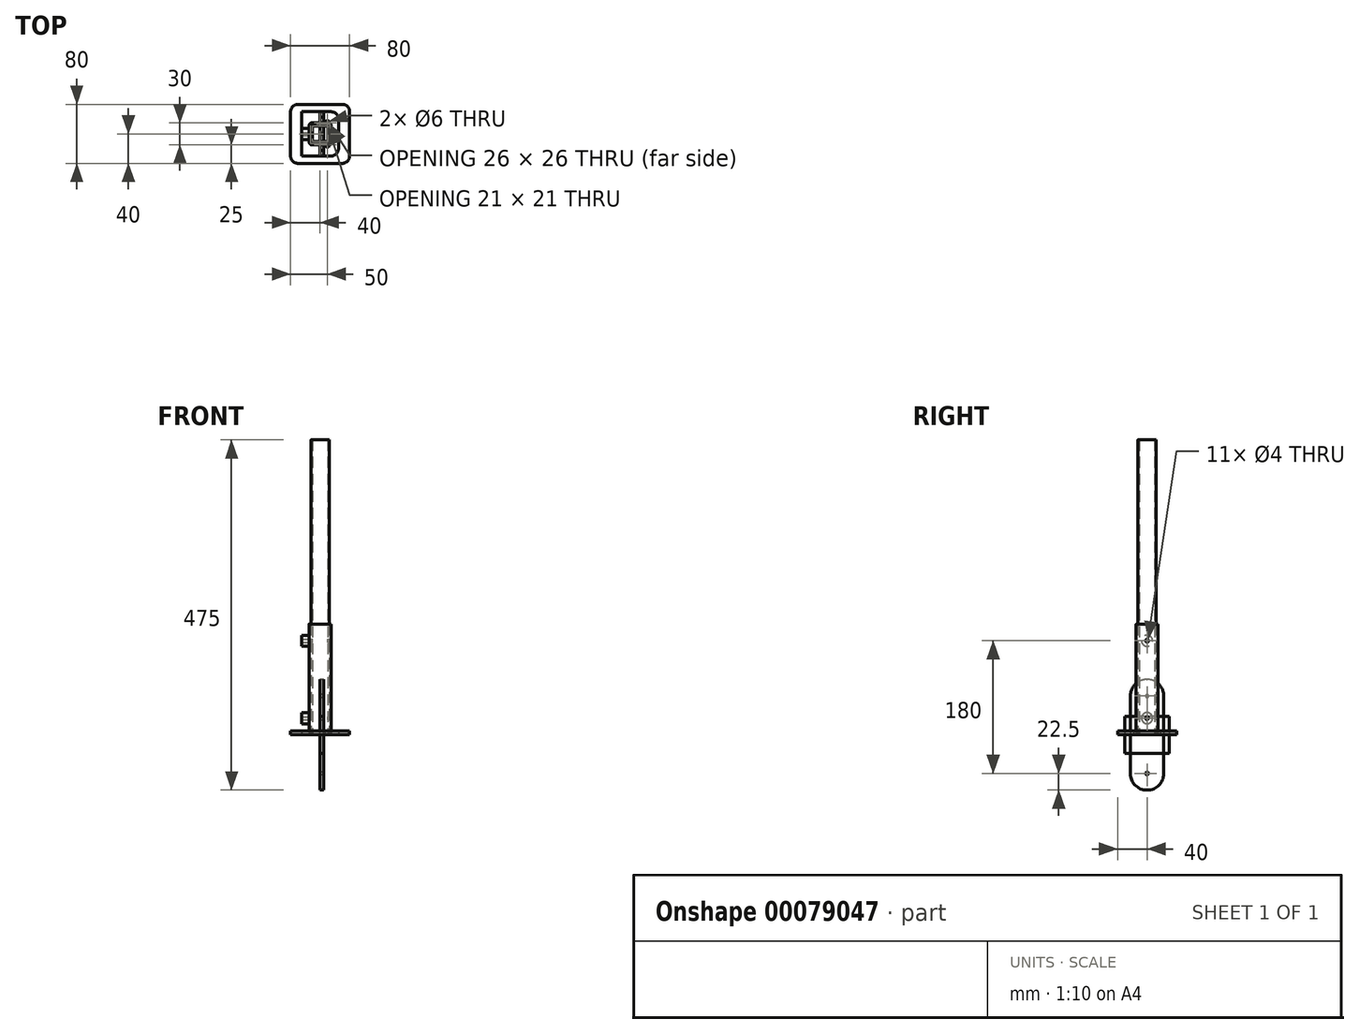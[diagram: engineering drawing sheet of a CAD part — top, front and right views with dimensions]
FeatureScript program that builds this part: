
annotation { "Feature Type Name" : "Feature", "Feature Type Description" : "" }
export const myFeature = defineFeature(function(context is Context, id is Id, definition is map)
    precondition{}
    {
        {
            var Q0;
            Q0=qCreatedBy(makeId("Top.planeOp"),FACE);
            var sketch = newSketch(context, id + "F0", { "sketchPlane" : qUnion([Q0])});
            skLineSegment(sketch, "E0.bottom", {"start": v(-30, -40) * mm, "end": v(30, -40) * mm});
            skLineSegment(sketch, "E0.top", {"start": v(-30, 40) * mm, "end": v(30, 40) * mm});
            skLineSegment(sketch, "E0.left", {"start": v(-40, -30) * mm, "end": v(-40, 30) * mm});
            skLineSegment(sketch, "E0.right", {"start": v(40, -30) * mm, "end": v(40, 30) * mm});
            skLineSegment(sketch, "E1", {"start": v(-40, 40) * mm, "end": v(40, -40) * mm, "construction": true});
            skPoint(sketch, "E2.visualSharp", {"position": v(40, 40) * mm});
            skArc(sketch, "E2.filletArc", {"start": v(40, 30) * mm, "mid": v(37.07, 37.07) * mm, "end": v(30, 40) * mm});
            skPoint(sketch, "E3.visualSharp", {"position": v(40, -40) * mm});
            skArc(sketch, "E3.filletArc", {"start": v(30, -40) * mm, "mid": v(37.07, -37.07) * mm, "end": v(40, -30) * mm});
            skPoint(sketch, "E4.visualSharp", {"position": v(-40, -40) * mm});
            skArc(sketch, "E4.filletArc", {"start": v(-40, -30) * mm, "mid": v(-37.07, -37.07) * mm, "end": v(-30, -40) * mm});
            skPoint(sketch, "E5.visualSharp", {"position": v(-40, 40) * mm});
            skArc(sketch, "E5.filletArc", {"start": v(-30, 40) * mm, "mid": v(-37.07, 37.07) * mm, "end": v(-40, 30) * mm});
            skSolve(sketch);
        }
        {
            var Q0;
            Q0=makeQuery(id+"F0.imprint","IMPRINT",FACE,{"disambiguationData":[TD([[makeQuery(id+"F0.imprint","IMPRINT",EDGE,{"derivedFrom":sQuery(id+"F0.wireOp",EDGE,"E0.bottom")}),1.0]])]});
            extrude(context, id + "F1", {"entities" : qUnion([Q0]), "depth" : 5 * mm});
        }
        {
            var Q0;
            Q0=qCreatedBy(makeId("Right.planeOp"),FACE);
            var sketch = newSketch(context, id + "F2", { "sketchPlane" : qUnion([Q0])});
            skLineSegment(sketch, "E6.bottom", {"start": v(30, -25) * mm, "end": v(-30, -25) * mm});
            skLineSegment(sketch, "E6.top", {"start": v(30, 25) * mm, "end": v(-30, 25) * mm});
            skLineSegment(sketch, "E6.left", {"start": v(30, -25) * mm, "end": v(30, 25) * mm});
            skLineSegment(sketch, "E6.right", {"start": v(-30, -25) * mm, "end": v(-30, 25) * mm});
            skLineSegment(sketch, "E7", {"start": v(30, 25) * mm, "end": v(-30, -25) * mm, "construction": true});
            skSolve(sketch);
        }
        {
            var Q0;
            Q0 = qSketchRegion(id + "F2", true);
            extrude(context, id + "F3", {"entities" : qUnion([Q0]), "depth" : 5 * mm});
        }
        {
            var Q0;
            Q0=qCreatedBy(makeId("Top.planeOp"),FACE);
            var sketch = newSketch(context, id + "F4", { "sketchPlane" : qUnion([Q0])});
            skLineSegment(sketch, "E8.bottom", {"start": v(15, 30) * mm, "end": v(-25, 30) * mm});
            skLineSegment(sketch, "E8.top", {"start": v(15, -30) * mm, "end": v(-25, -30) * mm});
            skLineSegment(sketch, "E8.left", {"start": v(25, 20) * mm, "end": v(25, -20) * mm});
            skLineSegment(sketch, "E8.right", {"start": v(-25, 30) * mm, "end": v(-25, -30) * mm});
            skLineSegment(sketch, "E9", {"start": v(25, 30) * mm, "end": v(-25, -30) * mm, "construction": true});
            skPoint(sketch, "E10.visualSharp", {"position": v(25, 30) * mm});
            skArc(sketch, "E10.filletArc", {"start": v(25, 20) * mm, "mid": v(22.07, 27.07) * mm, "end": v(15, 30) * mm});
            skPoint(sketch, "E11.visualSharp", {"position": v(25, -30) * mm});
            skArc(sketch, "E11.filletArc", {"start": v(15, -30) * mm, "mid": v(22.07, -27.07) * mm, "end": v(25, -20) * mm});
            skLineSegment(sketch, "E12", {"start": v(10, 30) * mm, "end": v(10, 15) * mm, "construction": true});
            skLineSegment(sketch, "E13", {"start": v(25, 15) * mm, "end": v(10, 15) * mm, "construction": true});
            skLineSegment(sketch, "E14", {"start": v(25, -15) * mm, "end": v(10, -15) * mm, "construction": true});
            skLineSegment(sketch, "E15", {"start": v(10, -30) * mm, "end": v(10, -15) * mm, "construction": true});
            skCircle(sketch, "E16", {"center": v(10, 15) * mm, "radius": 3 * mm});
            skCircle(sketch, "E17", {"center": v(10, -15) * mm, "radius": 3 * mm});
            skSolve(sketch);
        }
        {
            var Q0;
            Q0=makeQuery(id+"F4.imprint","IMPRINT",FACE,{"disambiguationData":[TD([[makeQuery(id+"F4.imprint","IMPRINT",EDGE,{"derivedFrom":sQuery(id+"F4.wireOp",EDGE,"E8.bottom")}),1.0]])]});
            extrude(context, id + "F5", {"entities" : qUnion([Q0]), "depth" : 5 * mm});
        }
        {
            var Q0;
            Q0=qCreatedBy(makeId("Top.planeOp"),FACE);
            var sketch = newSketch(context, id + "F6", { "sketchPlane" : qUnion([Q0])});
            skLineSegment(sketch, "E18.bottom", {"start": v(9.5, 12.5) * mm, "end": v(-9.5, 12.5) * mm});
            skLineSegment(sketch, "E18.top", {"start": v(9.5, -12.5) * mm, "end": v(-9.5, -12.5) * mm});
            skLineSegment(sketch, "E18.left", {"start": v(12.5, 9.5) * mm, "end": v(12.5, -9.5) * mm});
            skLineSegment(sketch, "E18.right", {"start": v(-12.5, 9.5) * mm, "end": v(-12.5, -9.5) * mm});
            skLineSegment(sketch, "E19", {"start": v(12.5, 12.5) * mm, "end": v(-12.5, -12.5) * mm, "construction": true});
            skPoint(sketch, "E20.visualSharp", {"position": v(12.5, 12.5) * mm});
            skArc(sketch, "E20.filletArc", {"start": v(12.5, 9.5) * mm, "mid": v(11.62, 11.62) * mm, "end": v(9.5, 12.5) * mm});
            skPoint(sketch, "E21.visualSharp", {"position": v(-12.5, 12.5) * mm});
            skArc(sketch, "E21.filletArc", {"start": v(-9.5, 12.5) * mm, "mid": v(-11.62, 11.62) * mm, "end": v(-12.5, 9.5) * mm});
            skPoint(sketch, "E22.visualSharp", {"position": v(-12.5, -12.5) * mm});
            skArc(sketch, "E22.filletArc", {"start": v(-12.5, -9.5) * mm, "mid": v(-11.62, -11.62) * mm, "end": v(-9.5, -12.5) * mm});
            skPoint(sketch, "E23.visualSharp", {"position": v(12.5, -12.5) * mm});
            skArc(sketch, "E23.filletArc", {"start": v(9.5, -12.5) * mm, "mid": v(11.62, -11.62) * mm, "end": v(12.5, -9.5) * mm});
            skArc(sketch, "E24.0", {"start": v(10.5, 9.5) * mm, "mid": v(10.2, 10.2) * mm, "end": v(9.5, 10.5) * mm});
            skLineSegment(sketch, "E24.1", {"start": v(9.5, 10.5) * mm, "end": v(-9.5, 10.5) * mm});
            skLineSegment(sketch, "E24.2", {"start": v(10.5, 9.5) * mm, "end": v(10.5, -9.5) * mm});
            skArc(sketch, "E24.3", {"start": v(-9.5, 10.5) * mm, "mid": v(-10.2, 10.2) * mm, "end": v(-10.5, 9.5) * mm});
            skArc(sketch, "E24.4", {"start": v(9.5, -10.5) * mm, "mid": v(10.2, -10.2) * mm, "end": v(10.5, -9.5) * mm});
            skLineSegment(sketch, "E24.5", {"start": v(9.5, -10.5) * mm, "end": v(-9.5, -10.5) * mm});
            skArc(sketch, "E24.6", {"start": v(-10.5, -9.5) * mm, "mid": v(-10.2, -10.2) * mm, "end": v(-9.5, -10.5) * mm});
            skLineSegment(sketch, "E24.7", {"start": v(-10.5, 9.5) * mm, "end": v(-10.5, -9.5) * mm});
            skSolve(sketch);
        }
        {
            var Q0;
            Q0=makeQuery(id+"F6.imprint","IMPRINT",FACE,{"disambiguationData":[TD([[makeQuery(id+"F6.imprint","IMPRINT",EDGE,{"derivedFrom":sQuery(id+"F6.wireOp",EDGE,"E18.bottom")}),1.0]])]});
            extrude(context, id + "F7", {"entities" : qUnion([Q0]), "depth" : 400 * mm});
        }
        {
            var Q0;
            Q0=qCreatedBy(makeId("Top.planeOp"),FACE);
            var sketch = newSketch(context, id + "F8", { "sketchPlane" : qUnion([Q0])});
            skLineSegment(sketch, "E25.bottom", {"start": v(11, 15) * mm, "end": v(-11, 15) * mm});
            skLineSegment(sketch, "E25.top", {"start": v(11, -15) * mm, "end": v(-11, -15) * mm});
            skLineSegment(sketch, "E25.left", {"start": v(15, 11) * mm, "end": v(15, -11) * mm});
            skLineSegment(sketch, "E25.right", {"start": v(-15, 11) * mm, "end": v(-15, -11) * mm});
            skLineSegment(sketch, "E26", {"start": v(15, 15) * mm, "end": v(-15, -15) * mm, "construction": true});
            skPoint(sketch, "E27.visualSharp", {"position": v(15, 15) * mm});
            skArc(sketch, "E27.filletArc", {"start": v(15, 11) * mm, "mid": v(13.83, 13.83) * mm, "end": v(11, 15) * mm});
            skPoint(sketch, "E28.visualSharp", {"position": v(-15, 15) * mm});
            skArc(sketch, "E28.filletArc", {"start": v(-11, 15) * mm, "mid": v(-13.83, 13.83) * mm, "end": v(-15, 11) * mm});
            skPoint(sketch, "E29.visualSharp", {"position": v(-15, -15) * mm});
            skArc(sketch, "E29.filletArc", {"start": v(-15, -11) * mm, "mid": v(-13.83, -13.83) * mm, "end": v(-11, -15) * mm});
            skPoint(sketch, "E30.visualSharp", {"position": v(15, -15) * mm});
            skArc(sketch, "E30.filletArc", {"start": v(11, -15) * mm, "mid": v(13.83, -13.83) * mm, "end": v(15, -11) * mm});
            skArc(sketch, "E31.0", {"start": v(13, 11) * mm, "mid": v(12.41, 12.41) * mm, "end": v(11, 13) * mm});
            skLineSegment(sketch, "E31.1", {"start": v(11, 13) * mm, "end": v(-11, 13) * mm});
            skLineSegment(sketch, "E31.2", {"start": v(13, 11) * mm, "end": v(13, -11) * mm});
            skArc(sketch, "E31.3", {"start": v(-11, 13) * mm, "mid": v(-12.41, 12.41) * mm, "end": v(-13, 11) * mm});
            skArc(sketch, "E31.4", {"start": v(11, -13) * mm, "mid": v(12.41, -12.41) * mm, "end": v(13, -11) * mm});
            skLineSegment(sketch, "E31.5", {"start": v(11, -13) * mm, "end": v(-11, -13) * mm});
            skArc(sketch, "E31.6", {"start": v(-13, -11) * mm, "mid": v(-12.41, -12.41) * mm, "end": v(-11, -13) * mm});
            skLineSegment(sketch, "E31.7", {"start": v(-13, 11) * mm, "end": v(-13, -11) * mm});
            skSolve(sketch);
        }
        {
            var Q0;
            Q0=makeQuery(id+"F8.imprint","IMPRINT",FACE,{"disambiguationData":[TD([[makeQuery(id+"F8.imprint","IMPRINT",EDGE,{"derivedFrom":sQuery(id+"F8.wireOp",EDGE,"E25.bottom")}),1.0]])]});
            extrude(context, id + "F9", {"entities" : qUnion([Q0]), "depth" : 150 * mm});
        }
        {
            var Q0;
            Q0=makeQuery(id+"F9.opExtrude","SWEPT_FACE",FACE,{"disambiguationData":[OSD([sQuery(id+"F8.wireOp",EDGE,"E25.left")])]});
            var sketch = newSketch(context, id + "F10", { "sketchPlane" : qUnion([Q0])});
            skCircle(sketch, "E32", {"center": v(0, 22.5) * mm, "radius": 2 * mm});
            skCircle(sketch, "E33", {"center": v(0, 127.5) * mm, "radius": 2 * mm});
            skLineSegment(sketch, "E34", {"start": v(0, 150) * mm, "end": v(0, 0) * mm, "construction": true});
            skLineSegment(sketch, "E35", {"start": v(11, 150) * mm, "end": v(0, 127.5) * mm, "construction": true});
            skLineSegment(sketch, "E36", {"start": v(-11, 0) * mm, "end": v(0, 22.5) * mm, "construction": true});
            skSolve(sketch);
        }
        {
            var Q0;
            Q0=makeQuery(id+"F10.imprint","IMPRINT",FACE,{"disambiguationData":[TD([[makeQuery(id+"F10.imprint","IMPRINT",EDGE,{"derivedFrom":sQuery(id+"F10.wireOp",EDGE,"E33")}),1.0]])]});
            var Q1;
            Q1=makeQuery(id+"F10.imprint","IMPRINT",FACE,{"disambiguationData":[TD([[makeQuery(id+"F10.imprint","IMPRINT",EDGE,{"derivedFrom":sQuery(id+"F10.wireOp",EDGE,"E32")}),1.0]])]});
            extrude(context, id + "F11", {"entities" : qUnion([Q0, Q1]), "operationType" : NewBodyOperationType.REMOVE, "oppositeDirection" : true, "depth" : 35 * mm});
        }
        {
            var Q0;
            Q0=makeQuery(id+"F9.opExtrude","SWEPT_FACE",FACE,{"disambiguationData":[OSD([sQuery(id+"F8.wireOp",EDGE,"E25.right")])]});
            var sketch = newSketch(context, id + "F12", { "sketchPlane" : qUnion([Q0])});
            skCircle(sketch, "E37", {"center": v(0, 127.5) * mm, "radius": 7.5 * mm});
            skCircle(sketch, "E38", {"center": v(0, 22.5) * mm, "radius": 7.5 * mm});
            skSolve(sketch);
        }
        {
            var Q0;
            Q0=makeQuery(id+"F12.imprint","IMPRINT",FACE,{"disambiguationData":[TD([[makeQuery(id+"F12.imprint","IMPRINT",EDGE,{"derivedFrom":sQuery(id+"F12.wireOp",EDGE,"E37")}),1.0]])]});
            var Q1;
            Q1=makeQuery(id+"F12.imprint","IMPRINT",FACE,{"disambiguationData":[TD([[makeQuery(id+"F12.imprint","IMPRINT",EDGE,{"derivedFrom":sQuery(id+"F12.wireOp",EDGE,"E38")}),1.0]])]});
            extrude(context, id + "F13", {"entities" : qUnion([Q0, Q1]), "operationType" : NewBodyOperationType.ADD, "depth" : 10 * mm});
        }
        {
            var Q0;
            Q0=qCreatedBy(makeId("Right.planeOp"),FACE);
            var sketch = newSketch(context, id + "F14", { "sketchPlane" : qUnion([Q0])});
            skLineSegment(sketch, "E39.bottom", {"start": v(-0.5, -75) * mm, "end": v(0.5, -75) * mm});
            skLineSegment(sketch, "E39.top", {"start": v(-0.5, 75) * mm, "end": v(0.5, 75) * mm});
            skLineSegment(sketch, "E39.left", {"start": v(-22.5, 53) * mm, "end": v(-22.5, -53) * mm});
            skLineSegment(sketch, "E39.right", {"start": v(22.5, 53) * mm, "end": v(22.5, -53) * mm});
            skLineSegment(sketch, "E40", {"start": v(0, 75) * mm, "end": v(0, -75) * mm, "construction": true});
            skPoint(sketch, "E41.visualSharp", {"position": v(-22.5, 75) * mm});
            skArc(sketch, "E41.filletArc", {"start": v(-0.5, 75) * mm, "mid": v(-16.06, 68.56) * mm, "end": v(-22.5, 53) * mm});
            skPoint(sketch, "E42.visualSharp", {"position": v(22.5, 75) * mm});
            skArc(sketch, "E42.filletArc", {"start": v(22.5, 53) * mm, "mid": v(16.06, 68.56) * mm, "end": v(0.5, 75) * mm});
            skPoint(sketch, "E43.visualSharp", {"position": v(22.5, -75) * mm});
            skArc(sketch, "E43.filletArc", {"start": v(0.5, -75) * mm, "mid": v(16.06, -68.56) * mm, "end": v(22.5, -53) * mm});
            skPoint(sketch, "E44.visualSharp", {"position": v(-22.5, -75) * mm});
            skArc(sketch, "E44.filletArc", {"start": v(-22.5, -53) * mm, "mid": v(-16.06, -68.56) * mm, "end": v(-0.5, -75) * mm});
            skCircle(sketch, "E45", {"center": v(0, 52.5) * mm, "radius": 2 * mm});
            skCircle(sketch, "E46", {"center": v(0, -52.5) * mm, "radius": 2 * mm});
            skLineSegment(sketch, "E47", {"start": v(-22.5, 75) * mm, "end": v(0, 52.5) * mm, "construction": true});
            skLineSegment(sketch, "E48", {"start": v(22.5, -75) * mm, "end": v(0, -52.5) * mm, "construction": true});
            skSolve(sketch);
        }
        {
            var Q0;
            Q0=makeQuery(id+"F14.imprint","IMPRINT",FACE,{"disambiguationData":[TD([[makeQuery(id+"F14.imprint","IMPRINT",EDGE,{"derivedFrom":sQuery(id+"F14.wireOp",EDGE,"E39.bottom")}),1.0]])]});
            extrude(context, id + "F15", {"entities" : qUnion([Q0]), "depth" : 5 * mm});
        }
    });
